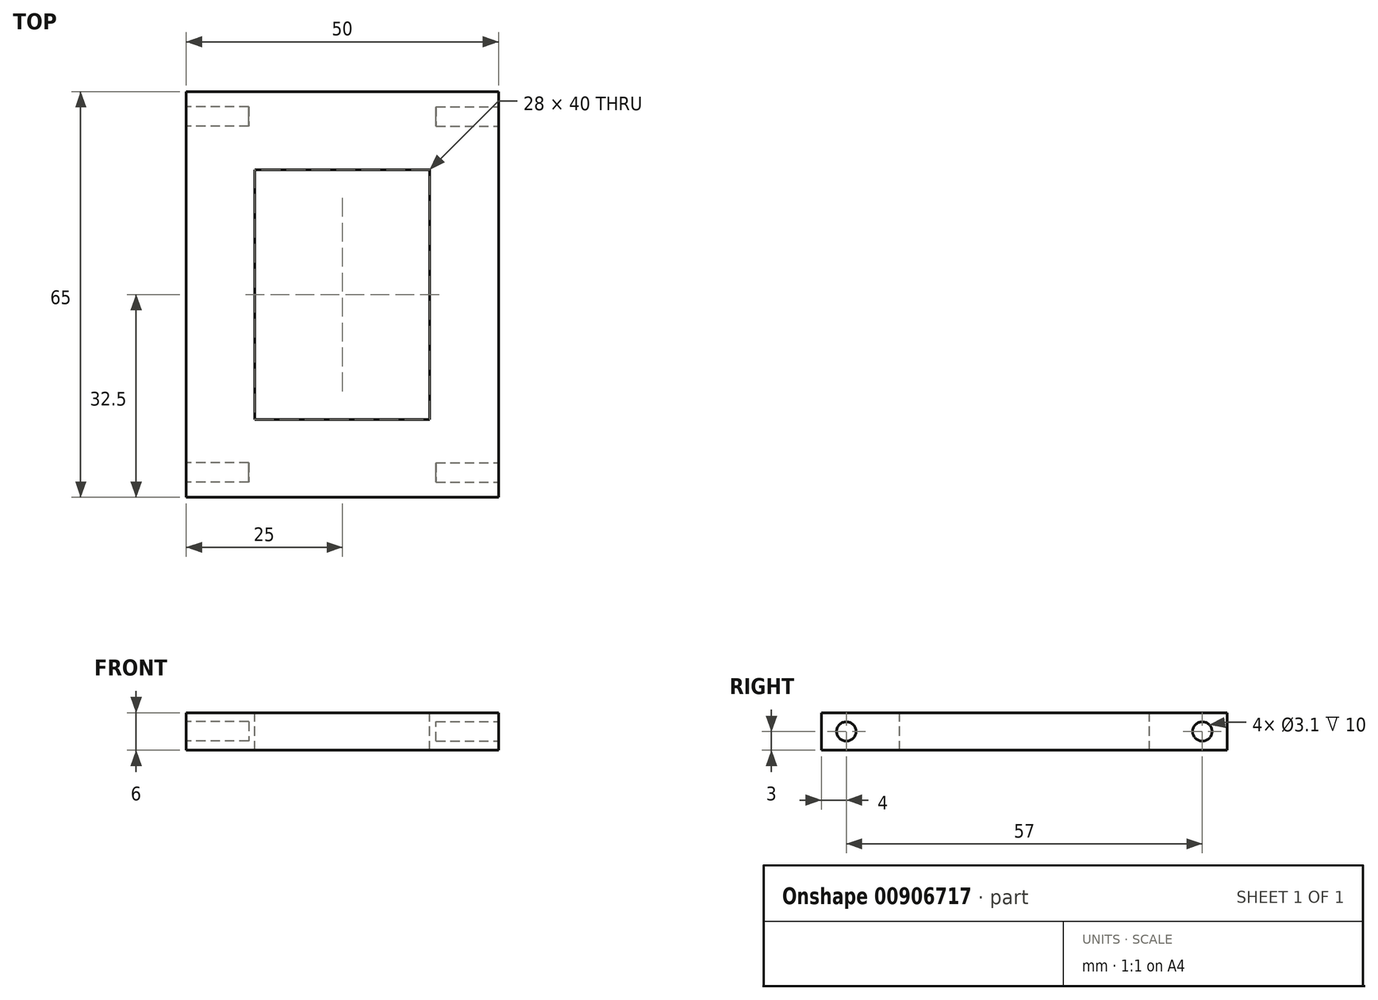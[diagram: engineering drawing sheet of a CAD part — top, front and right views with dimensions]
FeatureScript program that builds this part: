
annotation { "Feature Type Name" : "Feature", "Feature Type Description" : "" }
export const myFeature = defineFeature(function(context is Context, id is Id, definition is map)
    precondition{}
    {
        {
            var Q0;
            Q0=qCreatedBy(makeId("Top.planeOp"),FACE);
            var sketch = newSketch(context, id + "F0", { "sketchPlane" : qUnion([Q0])});
            skLineSegment(sketch, "E0.bottom", {"start": v(-25, 32.5) * mm, "end": v(25, 32.5) * mm});
            skLineSegment(sketch, "E0.top", {"start": v(-25, -32.5) * mm, "end": v(25, -32.5) * mm});
            skLineSegment(sketch, "E0.left", {"start": v(-25, 32.5) * mm, "end": v(-25, -32.5) * mm});
            skLineSegment(sketch, "E0.right", {"start": v(25, 32.5) * mm, "end": v(25, -32.5) * mm});
            skPoint(sketch, "E0.middle", {"position": v(0, 0) * mm});
            skSolve(sketch);
        }
        {
            var Q0;
            Q0 = qSketchRegion(id + "F0", true);
            extrude(context, id + "F1", {"entities" : qUnion([Q0]), "depth" : 6 * mm, "offsetDistance" : 25 * mm});
        }
        {
            var Q0;
            Q0=makeQuery(id+"F1.opExtrude","CAP_FACE",FACE,{"disambiguationData":[OSD([sQuery(id+"F0.wireOp",EDGE,"E0.bottom"),sQuery(id+"F0.wireOp",EDGE,"E0.top"),sQuery(id+"F0.wireOp",EDGE,"E0.left"),sQuery(id+"F0.wireOp",EDGE,"E0.right")])],"isStart":false});
            var sketch = newSketch(context, id + "F2", { "sketchPlane" : qUnion([Q0])});
            skLineSegment(sketch, "E1.bottom", {"start": v(-14, 20) * mm, "end": v(14, 20) * mm});
            skLineSegment(sketch, "E1.top", {"start": v(-14, -20) * mm, "end": v(14, -20) * mm});
            skLineSegment(sketch, "E1.left", {"start": v(-14, 20) * mm, "end": v(-14, -20) * mm});
            skLineSegment(sketch, "E1.right", {"start": v(14, 20) * mm, "end": v(14, -20) * mm});
            skPoint(sketch, "E1.middle", {"position": v(0, 0) * mm});
            skSolve(sketch);
        }
        {
            var Q0;
            Q0=makeQuery(id+"F2.imprint","IMPRINT",FACE,{"disambiguationData":[TD([[makeQuery(id+"F2.imprint","IMPRINT",EDGE,{"derivedFrom":sQuery(id+"F2.wireOp",EDGE,"E1.bottom")}),-1.0]])]});
            extrude(context, id + "F3", {"entities" : qUnion([Q0]), "operationType" : NewBodyOperationType.REMOVE, "oppositeDirection" : true, "depth" : 25 * mm, "offsetDistance" : 25 * mm});
        }
        {
            var Q0;
            Q0=makeQuery(id+"F1.opExtrude","SWEPT_FACE",FACE,{"disambiguationData":[OSD([sQuery(id+"F0.wireOp",EDGE,"E0.right")])]});
            var sketch = newSketch(context, id + "F4", { "sketchPlane" : qUnion([Q0])});
            skLineSegment(sketch, "E2", {"start": v(-32.5, 3) * mm, "end": v(-28.5, 3) * mm});
            skCircle(sketch, "E3", {"center": v(-28.5, 3) * mm, "radius": 1.55 * mm});
            skLineSegment(sketch, "E4", {"start": v(32.5, 3) * mm, "end": v(28.5, 3) * mm});
            skCircle(sketch, "E5", {"center": v(28.5, 3) * mm, "radius": 1.55 * mm});
            skSolve(sketch);
        }
        {
            var Q0;
            Q0 = qSketchRegion(id + "F4", true);
            extrude(context, id + "F5", {"entities" : qUnion([Q0]), "operationType" : NewBodyOperationType.REMOVE, "oppositeDirection" : true, "depth" : 10 * mm, "offsetDistance" : 25 * mm});
        }
        {
            var Q0;
            Q0=makeQuery(id+"F1.opExtrude","SWEPT_FACE",FACE,{"disambiguationData":[OSD([sQuery(id+"F0.wireOp",EDGE,"E0.left")])]});
            var sketch = newSketch(context, id + "F6", { "sketchPlane" : qUnion([Q0])});
            skLineSegment(sketch, "E6", {"start": v(-32.5, 3) * mm, "end": v(-28.5, 3) * mm});
            skCircle(sketch, "E7", {"center": v(-28.5, 3) * mm, "radius": 1.55 * mm});
            skLineSegment(sketch, "E8", {"start": v(32.5, 3) * mm, "end": v(28.5, 3) * mm});
            skCircle(sketch, "E9", {"center": v(28.5, 3) * mm, "radius": 1.55 * mm});
            skSolve(sketch);
        }
        {
            var Q0;
            Q0 = qSketchRegion(id + "F6", true);
            extrude(context, id + "F7", {"entities" : qUnion([Q0]), "operationType" : NewBodyOperationType.REMOVE, "oppositeDirection" : true, "depth" : 10 * mm, "offsetDistance" : 25 * mm});
        }
    });
